# Revit family: result
name_source: partatom
category: Plumbing Fixtures
revit_build: Autodesk Revit 2015 (Build: 20140903_1530(x64)
units: mm (PartAtom-declared; Revit-internal decimal feet)

## types (1)
- Default
    BIMobject category = Taps & Mixers
    BIMobject category code = sanitary-taps-mixers
    BIMobject main category = Sanitary
    BIMobject main category code = sanitary
    Brand url = http://www.duravit.com
    Edition number = 1
    GTIN code = https://4053424865645
    Installation instructions = https://pro.duravit.com
    Manufacturer name = DURAVIT
    Product Guid = b2b9f6ef-80cd-4865-9dd2-6caf7bf33522
    Product SKU = a1-single-lever-washbasin-mixer-a11010002
    Product certification = https://pro.duravit.com
    Product data url = https://bimobject.com
    Product family = A.1
    Product group = Sink fittings
    Product name = A11010002-A.1 Single lever washbasin mixer
    Product url = https://pro.duravit.com
    QR code = http://bimobject.com
    Technical description = https://pro.duravit.com
    Youtube clip = https://pro.duravit.com

## geometry (parser evidence)
native form markers: Sweep x3
no freeform markers — native parametric forms only
